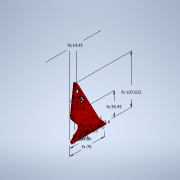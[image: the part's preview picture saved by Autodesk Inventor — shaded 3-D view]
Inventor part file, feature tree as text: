
AUTODESK INVENTOR PART (.ipt)
format: ipt  version: 2020 (Build 240168000, 168)  size: 534,528 bytes
history: native  units: mm
features: extrude x3, fillet x3, sketch x3, projected_geometry x1
ambient origin geometry x8: Origin, YZ Plane, XZ Plane, XY Plane, X Axis, Y Axis, Z Axis, Center Point
bodies: Solid1 (feature_tree)
feature tree (10):
  extrude  "Extrusion1"  Depth=27.0mm
  extrude  "Extrusion9"  Depth=27.8mm
  fillet  "Fillet2"  Radius=50.45mm
  fillet  "Fillet3"  Radius=10.0mm
  extrude  "Extrusion8"  Depth=6.8mm
  fillet  "Fillet4"  Radius=1.6mm
  sketch  "Sketch1"  dims[d0=45.0deg d1=27.0mm]
  sketch  "Sketch8"  dims[d5=5.0mm d6=0.0mm d34=27.8mm d40=50.45mm d47=10.0mm]
  projected_geometry  "Projected Loop6"
  sketch  "Sketch9"  dims[d55=4.8mm d56=6.8mm d57=1.6mm d58=30.0mm d60=16.333333mm d61=10.0mm d63=10.0mm d65=5.0mm d66=10.0mm d67=107.032605mm d71=3.0mm d72=3.0mm d75=0.5mm d76=3.6mm d77=12.0mm d78=20.0mm d79=0.0mm d80=0.0mm d81=49.0mm d88=2.0mm d94=1.5mm d95=1.5mm d96=1.5mm d97=1.5mm d98=3.0mm d99=0.0mm d100=14.45mm d102=76.0mm d103=3.1mm d104=10.0mm d105=30.0mm d106=3.1mm d108=56.0mm d109=10.0mm d110=6.108652mm d112=7.0mm d50=0.5mm d51=0.872665mm d52=0.5mm d53=0.872665mm d111=0.872665mm d113=0.872665mm]
